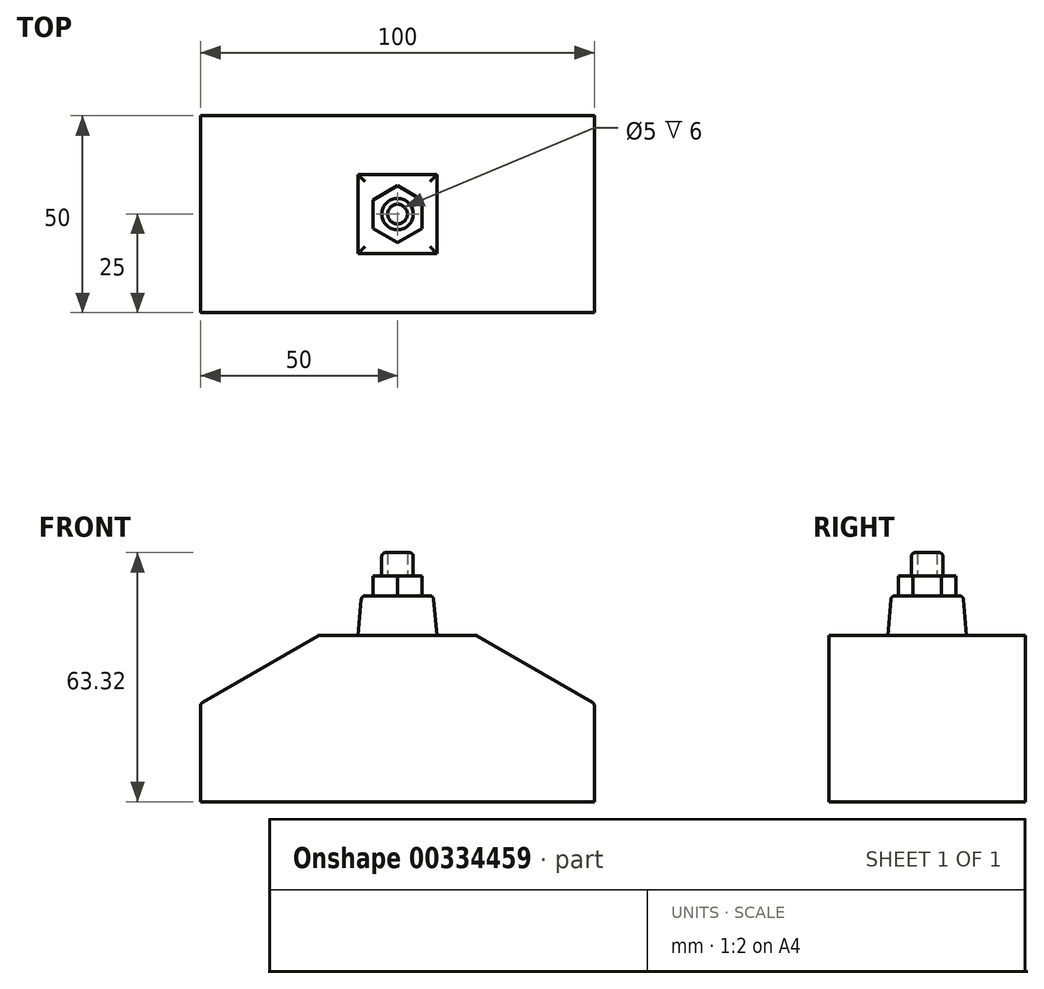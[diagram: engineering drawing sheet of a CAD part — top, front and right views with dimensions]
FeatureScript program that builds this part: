
annotation { "Feature Type Name" : "Feature", "Feature Type Description" : "" }
export const myFeature = defineFeature(function(context is Context, id is Id, definition is map)
    precondition{}
    {
        {
            var Q0;
            Q0=qCreatedBy(makeId("Front.planeOp"),FACE);
            var sketch = newSketch(context, id + "F0", { "sketchPlane" : qUnion([Q0])});
            skLineSegment(sketch, "E0", {"start": v(0, 0) * mm, "end": v(50, 0) * mm});
            skLineSegment(sketch, "E1", {"start": v(50, 0) * mm, "end": v(50, 25) * mm});
            skLineSegment(sketch, "E2", {"start": v(-50, 25) * mm, "end": v(-50, 0) * mm});
            skLineSegment(sketch, "E3", {"start": v(-50, 0) * mm, "end": v(0, 0) * mm});
            skLineSegment(sketch, "E4", {"start": v(-50, 25) * mm, "end": v(-20, 42.32) * mm});
            skLineSegment(sketch, "E5", {"start": v(-20, 42.32) * mm, "end": v(20, 42.32) * mm});
            skLineSegment(sketch, "E6", {"start": v(20, 42.32) * mm, "end": v(50, 25) * mm});
            skSolve(sketch);
        }
        {
            var Q0;
            Q0=makeQuery(id+"F0.imprint","IMPRINT",FACE,{"disambiguationData":[TD([[makeQuery(id+"F0.imprint","IMPRINT",EDGE,{"derivedFrom":sQuery(id+"F0.wireOp",EDGE,"E0")}),1.0]])]});
            extrude(context, id + "F1", {"entities" : qUnion([Q0]), "depth" : 50 * mm, "symmetric" : true});
        }
        {
            var Q0;
            Q0=makeQuery(id+"F1.opExtrude","SWEPT_FACE",FACE,{"disambiguationData":[OSD([sQuery(id+"F0.wireOp",EDGE,"E5")])]});
            var sketch = newSketch(context, id + "F2", { "sketchPlane" : qUnion([Q0])});
            skLineSegment(sketch, "E7.bottom", {"start": v(10, 10) * mm, "end": v(-10, 10) * mm});
            skLineSegment(sketch, "E7.top", {"start": v(10, -10) * mm, "end": v(-10, -10) * mm});
            skLineSegment(sketch, "E7.left", {"start": v(10, 10) * mm, "end": v(10, -10) * mm});
            skLineSegment(sketch, "E7.right", {"start": v(-10, 10) * mm, "end": v(-10, -10) * mm});
            skPoint(sketch, "E7.middle", {"position": v(0, 0) * mm});
            skSolve(sketch);
        }
        {
            var Q0;
            Q0=makeQuery(id+"F2.imprint","IMPRINT",FACE,{"disambiguationData":[TD([[makeQuery(id+"F2.imprint","IMPRINT",EDGE,{"derivedFrom":sQuery(id+"F2.wireOp",EDGE,"E7.bottom")}),1.0]])]});
            extrude(context, id + "F3", {"entities" : qUnion([Q0]), "operationType" : NewBodyOperationType.ADD, "depth" : 10 * mm, "hasDraft" : true, "draftAngle" : 5 * degree, "draftPullDirection" : true});
        }
        {
            var Q0;
            Q0=makeQuery(id+"F3.opExtrude","CAP_FACE",FACE,{"disambiguationData":[OSD([sQuery(id+"F2.wireOp",EDGE,"E7.bottom"),sQuery(id+"F2.wireOp",EDGE,"E7.top"),sQuery(id+"F2.wireOp",EDGE,"E7.left"),sQuery(id+"F2.wireOp",EDGE,"E7.right")])],"isStart":false});
            var sketch = newSketch(context, id + "F4", { "sketchPlane" : qUnion([Q0])});
            skCircle(sketch, "E8.cCircle", {"center": v(0, 0) * mm, "radius": 7.25 * mm, "construction": true});
            skLineSegment(sketch, "E8.0", {"start": v(0, 7.25) * mm, "end": v(6.28, 3.63) * mm});
            skLineSegment(sketch, "E8.1", {"start": v(6.28, 3.63) * mm, "end": v(6.28, -3.62) * mm});
            skLineSegment(sketch, "E8.2", {"start": v(6.28, -3.62) * mm, "end": v(0, -7.25) * mm});
            skLineSegment(sketch, "E8.3", {"start": v(0, -7.25) * mm, "end": v(-6.28, -3.63) * mm});
            skLineSegment(sketch, "E8.4", {"start": v(-6.28, -3.63) * mm, "end": v(-6.28, 3.62) * mm});
            skLineSegment(sketch, "E8.5", {"start": v(-6.28, 3.62) * mm, "end": v(0, 7.25) * mm});
            skSolve(sketch);
        }
        {
            var Q0;
            Q0=makeQuery(id+"F4.imprint","IMPRINT",FACE,{"disambiguationData":[TD([[makeQuery(id+"F4.imprint","IMPRINT",EDGE,{"derivedFrom":sQuery(id+"F4.wireOp",EDGE,"E8.0")}),-1.0]])]});
            extrude(context, id + "F5", {"entities" : qUnion([Q0]), "operationType" : NewBodyOperationType.ADD, "depth" : 5 * mm});
        }
        {
            var Q0;
            Q0=makeQuery(id+"F5.opExtrude","CAP_FACE",FACE,{"disambiguationData":[OSD([sQuery(id+"F4.wireOp",EDGE,"E8.0"),sQuery(id+"F4.wireOp",EDGE,"E8.1"),sQuery(id+"F4.wireOp",EDGE,"E8.2"),sQuery(id+"F4.wireOp",EDGE,"E8.3"),sQuery(id+"F4.wireOp",EDGE,"E8.4"),sQuery(id+"F4.wireOp",EDGE,"E8.5")])],"isStart":false});
            var sketch = newSketch(context, id + "F6", { "sketchPlane" : qUnion([Q0])});
            skCircle(sketch, "E9", {"center": v(0, 0) * mm, "radius": 4 * mm});
            skPoint(sketch, "E9.first.point", {"position": v(-4, 0) * mm});
            skPoint(sketch, "E9.second.point", {"position": v(4, 0) * mm});
            skPoint(sketch, "E9.third.point", {"position": v(0, -4) * mm});
            skCircle(sketch, "E10.0", {"center": v(0, 0) * mm, "radius": 2.5 * mm});
            skSolve(sketch);
        }
        {
            var Q0;
            Q0=makeQuery(id+"F6.imprint","IMPRINT",FACE,{"disambiguationData":[TD([[makeQuery(id+"F6.imprint","IMPRINT",EDGE,{"derivedFrom":sQuery(id+"F6.wireOp",EDGE,"E9")}),1.0]])]});
            extrude(context, id + "F7", {"entities" : qUnion([Q0]), "operationType" : NewBodyOperationType.ADD, "depth" : 6 * mm});
        }
        {
            var Q0;
            Q0=makeQuery(id+"F7.boolean.opBoolean","SPLIT",FACE,{"disambiguationData":[TD([makeQuery(id+"F7.opExtrude","SWEPT_FACE",FACE,{"disambiguationData":[OSD([sQuery(id+"F6.wireOp",EDGE,"E10.0")])]})])],"derivedFrom":makeQuery(id+"F5.opExtrude","CAP_FACE",FACE,{"disambiguationData":[OSD([sQuery(id+"F4.wireOp",EDGE,"E8.0"),sQuery(id+"F4.wireOp",EDGE,"E8.1"),sQuery(id+"F4.wireOp",EDGE,"E8.2"),sQuery(id+"F4.wireOp",EDGE,"E8.3"),sQuery(id+"F4.wireOp",EDGE,"E8.4"),sQuery(id+"F4.wireOp",EDGE,"E8.5")])],"isStart":false})});
            extrude(context, id + "F8", {"entities" : qUnion([Q0]), "operationType" : NewBodyOperationType.ADD, "oppositeDirection" : true, "depth" : 45 * mm});
        }
        {
            var Q0;
            Q0=makeQuery(id+"F3.opExtrude","CAP_EDGE",EDGE,{"disambiguationData":[OSD([sQuery(id+"F2.wireOp",EDGE,"E7.left")])],"isStart":false});
            var Q1;
            Q1=makeQuery(id+"F3.opExtrude","CAP_EDGE",EDGE,{"disambiguationData":[OSD([sQuery(id+"F2.wireOp",EDGE,"E7.top")])],"isStart":false});
            var Q2;
            Q2=makeQuery(id+"F3.opExtrude","CAP_EDGE",EDGE,{"disambiguationData":[OSD([sQuery(id+"F2.wireOp",EDGE,"E7.right")])],"isStart":false});
            var Q3;
            Q3=makeQuery(id+"F3.opExtrude","CAP_EDGE",EDGE,{"disambiguationData":[OSD([sQuery(id+"F2.wireOp",EDGE,"E7.bottom")])],"isStart":false});
            fillet(context, id + "F9", {"entities" : qUnion([Q0, Q1, Q2, Q3]), "radius" : 1 * mm, "tangentPropagation" : true, "allowEdgeOverflow" : false});
        }
        {
            var Q0;
            Q0=makeQuery(id+"F7.opExtrude","CAP_EDGE",EDGE,{"disambiguationData":[OSD([sQuery(id+"F6.wireOp",EDGE,"E9")])],"isStart":false});
            fillet(context, id + "F10", {"entities" : qUnion([Q0]), "radius" : 1 * mm, "tangentPropagation" : true, "allowEdgeOverflow" : false});
        }
        {
            var Q0;
            Q0=makeQuery(id+"F1.opExtrude","SWEPT_EDGE",EDGE,{"disambiguationData":[OSD([sQuery(id+"F0.wireOp",EDGE,"E4"),sQuery(id+"F0.wireOp",EDGE,"E5")])]});
            var Q1;
            Q1=makeQuery(id+"F1.opExtrude","SWEPT_EDGE",EDGE,{"disambiguationData":[OSD([sQuery(id+"F0.wireOp",EDGE,"E5"),sQuery(id+"F0.wireOp",EDGE,"E6")])]});
            var Q2;
            Q2=makeQuery(id+"F1.opExtrude","SWEPT_EDGE",EDGE,{"disambiguationData":[OSD([sQuery(id+"F0.wireOp",EDGE,"E1"),sQuery(id+"F0.wireOp",EDGE,"E6")])]});
            var Q3;
            Q3=makeQuery(id+"F1.opExtrude","SWEPT_EDGE",EDGE,{"disambiguationData":[OSD([sQuery(id+"F0.wireOp",EDGE,"E2"),sQuery(id+"F0.wireOp",EDGE,"E4")])]});
            fillet(context, id + "F11", {"entities" : qUnion([Q0, Q1, Q2, Q3]), "radius" : 1 * mm, "tangentPropagation" : true, "allowEdgeOverflow" : false});
        }
    });
